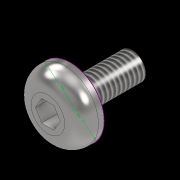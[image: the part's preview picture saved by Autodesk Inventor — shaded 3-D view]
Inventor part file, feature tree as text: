
AUTODESK INVENTOR PART (.ipt)
format: ipt  version: 2022.2 (Build 262287010, 287A)  size: 138,240 bytes
history: native  units: mm
features: extrude x3, sketch x2, fillet x2, thread x1
ambient origin geometry x8: Origin, YZ Plane, XZ Plane, XY Plane, X Axis, Y Axis, Z Axis, Center Point
bodies: Solid1 (feature_tree)
feature tree (8):
  sketch  "Sketch1"  dims[d0=4.8mm d1=12.0mm]
  extrude  "Extrusion1"  Depth=12.0mm
  extrude  "Extrusion2"  Depth=11.0mm TaperAngle=0.0deg
  fillet  "Fillet1"  Radius=1.0mm
  fillet  "Fillet2"  Radius=3.0mm
  extrude  "Extrusion3"  Depth=10.0mm
  thread  "Thread1"  [1 undecoded]
  sketch  "Sketch2"  dims[d2=4.0mm d3=0.0mm d4=11.0mm d5=0.0mm d6=1.0mm d7=3.0mm d8=4.4mm d9=3.0mm d10=0.0mm d11=10.0mm d12=0.0mm]
note: 1 required parameter value undecoded (feature->parameter linkage not recoverable at this tier; creation-order binding heuristic only, values carry confidence <= 0.55)
